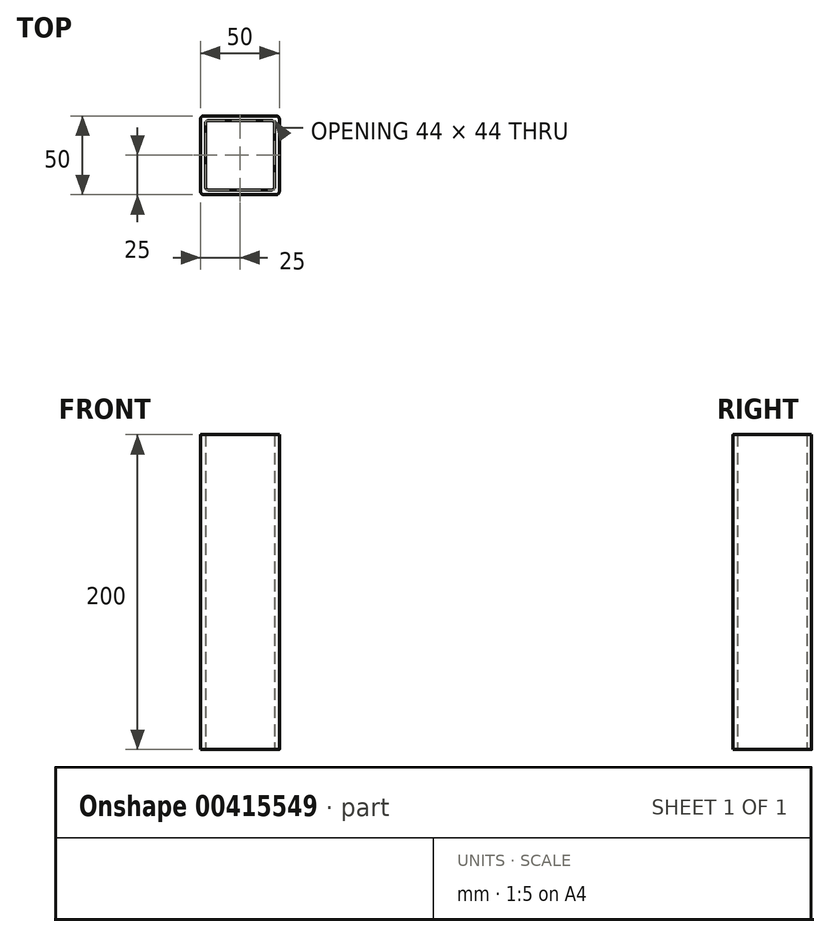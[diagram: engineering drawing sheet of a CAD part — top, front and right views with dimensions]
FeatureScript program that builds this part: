
annotation { "Feature Type Name" : "Feature", "Feature Type Description" : "" }
export const myFeature = defineFeature(function(context is Context, id is Id, definition is map)
    precondition{}
    {
        {
            var Q0;
            Q0=qCreatedBy(makeId("Top.planeOp"),FACE);
            var sketch = newSketch(context, id + "F0", { "sketchPlane" : qUnion([Q0])});
            skLineSegment(sketch, "E0.bottom", {"start": v(23, 25) * mm, "end": v(-23, 25) * mm});
            skLineSegment(sketch, "E0.top", {"start": v(23, -25) * mm, "end": v(-23, -25) * mm});
            skLineSegment(sketch, "E0.left", {"start": v(25, 23) * mm, "end": v(25, -23) * mm});
            skLineSegment(sketch, "E0.right", {"start": v(-25, 23) * mm, "end": v(-25, -23) * mm});
            skPoint(sketch, "E0.middle", {"position": v(0, 0) * mm});
            skLineSegment(sketch, "E1.bottom", {"start": v(20, 22) * mm, "end": v(-20, 22) * mm});
            skLineSegment(sketch, "E1.top", {"start": v(20, -22) * mm, "end": v(-20, -22) * mm});
            skLineSegment(sketch, "E1.left", {"start": v(22, 20) * mm, "end": v(22, -20) * mm});
            skLineSegment(sketch, "E1.right", {"start": v(-22, 20) * mm, "end": v(-22, -20) * mm});
            skPoint(sketch, "E2.visualSharp", {"position": v(-22, 22) * mm});
            skArc(sketch, "E2.filletArc", {"start": v(-20, 22) * mm, "mid": v(-21.41, 21.41) * mm, "end": v(-22, 20) * mm});
            skPoint(sketch, "E3.visualSharp", {"position": v(-22, -22) * mm});
            skArc(sketch, "E3.filletArc", {"start": v(-22, -20) * mm, "mid": v(-21.41, -21.41) * mm, "end": v(-20, -22) * mm});
            skPoint(sketch, "E4.visualSharp", {"position": v(22, -22) * mm});
            skArc(sketch, "E4.filletArc", {"start": v(20, -22) * mm, "mid": v(21.41, -21.41) * mm, "end": v(22, -20) * mm});
            skPoint(sketch, "E5.visualSharp", {"position": v(22, 22) * mm});
            skArc(sketch, "E5.filletArc", {"start": v(22, 20) * mm, "mid": v(21.41, 21.41) * mm, "end": v(20, 22) * mm});
            skPoint(sketch, "E6.visualSharp", {"position": v(-25, -25) * mm});
            skArc(sketch, "E6.filletArc", {"start": v(-25, -23) * mm, "mid": v(-24.41, -24.41) * mm, "end": v(-23, -25) * mm});
            skPoint(sketch, "E7.visualSharp", {"position": v(-25, 25) * mm});
            skArc(sketch, "E7.filletArc", {"start": v(-23, 25) * mm, "mid": v(-24.41, 24.41) * mm, "end": v(-25, 23) * mm});
            skPoint(sketch, "E8.visualSharp", {"position": v(25, 25) * mm});
            skArc(sketch, "E8.filletArc", {"start": v(25, 23) * mm, "mid": v(24.41, 24.41) * mm, "end": v(23, 25) * mm});
            skPoint(sketch, "E9.visualSharp", {"position": v(25, -25) * mm});
            skArc(sketch, "E9.filletArc", {"start": v(23, -25) * mm, "mid": v(24.41, -24.41) * mm, "end": v(25, -23) * mm});
            skSolve(sketch);
        }
        {
            var Q0;
            Q0 = qSketchRegion(id + "F0", true);
            extrude(context, id + "F1", {"entities" : qUnion([Q0]), "depth" : 200 * mm});
        }
    });
